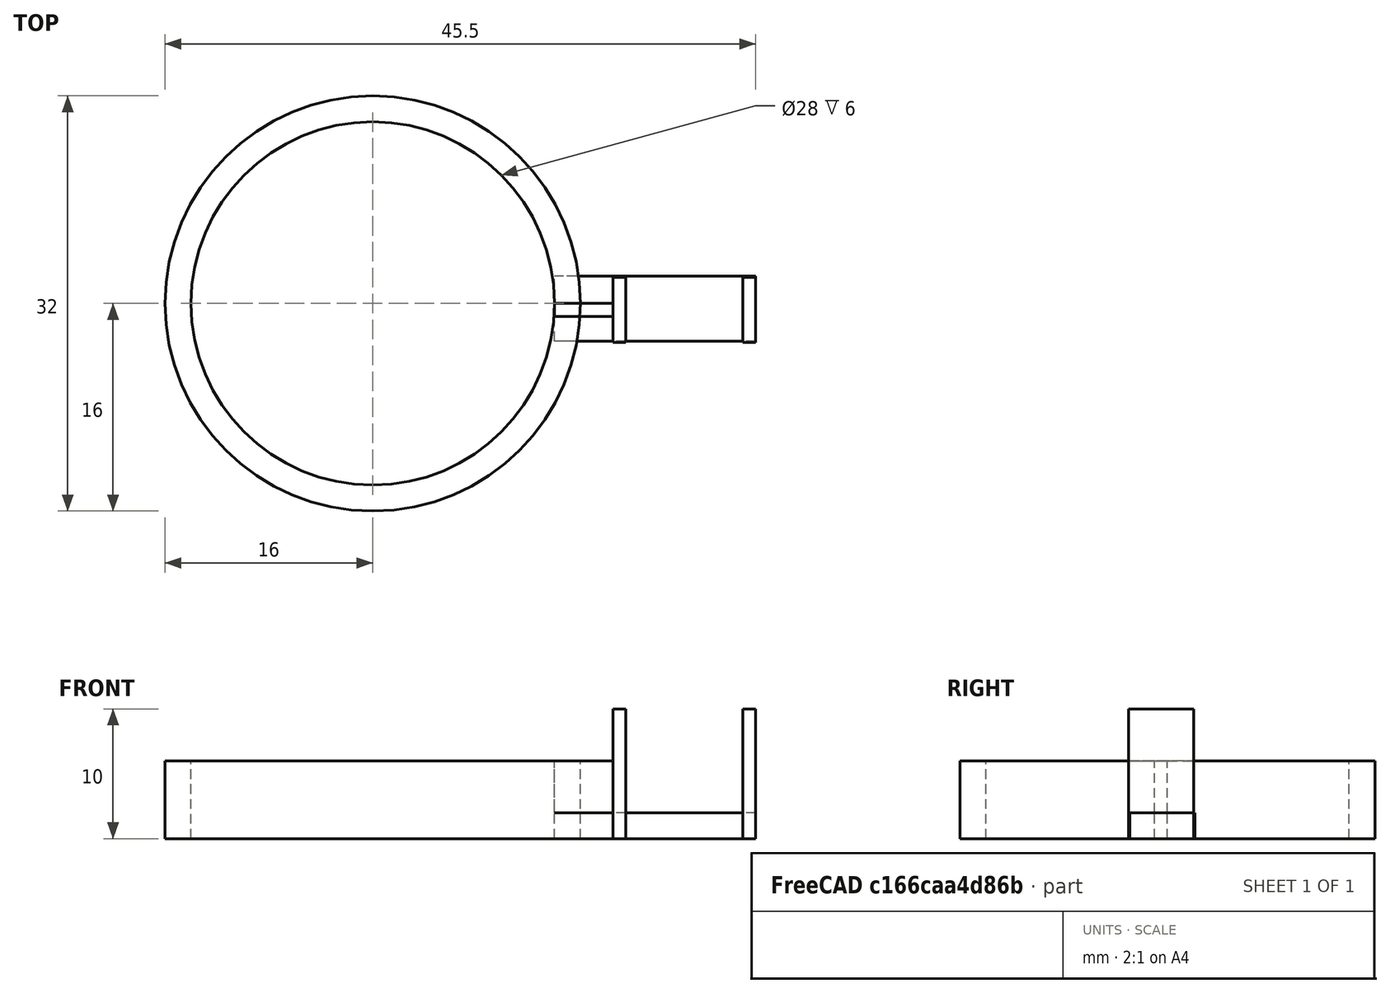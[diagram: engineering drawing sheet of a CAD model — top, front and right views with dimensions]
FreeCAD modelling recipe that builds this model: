
FCSTD DOCUMENT  (FreeCAD 0.18R16117 (Git))
Label: tf2
License: All rights reserved
LicenseURL: http://en.wikipedia.org/wiki/All_rights_reserved
objects: App::MeasureDistance×7, Part::Box×4, Part::Cylinder×2, Part::Cut×1, Part::FeaturePython×1, Part::Mirroring×1
note: 9 computed .brp shape members not serialized (recipe doc carries the construction recipe); baked Part::Feature solids carry a one-line shape summary decoded from their .brp

FEATURE [Part::Cylinder] Cylinder  label="Outer"
  Angle = 360
  AttacherType = Attacher::AttachEngine3D
  Height = 6
  Radius = 16
FEATURE [Part::Cylinder] Cylinder001  label="Inner"
  Angle = 360
  AttacherType = Attacher::AttachEngine3D
  Height = 6
  Radius = 14
FEATURE [Part::Cut] Cut  label="Ring"
  Base = -> Cylinder
  Tool = -> Cylinder001
FEATURE [Part::Box] Box002  label="Cube002"
  AttacherType = Attacher::AttachEngine3D
  Height = 10
  Length = 1
  Placement = pos=(-24,-3,0) rot=(0,0,1;0rad)
  Width = 5
FEATURE [Part::Box] Box003  label="Cube003"
  AttacherType = Attacher::AttachEngine3D
  Height = 6
  Length = 1
  Placement = pos=(-23,7e-15,0) rot=(0,0,-1;1.5708rad)
  Width = 4.5
FEATURE [Part::Box] Box  label="Cube"
  AttacherType = Attacher::AttachEngine3D
  Height = 2
  Length = 15.5
  Placement = pos=(-34,-2.9,0) rot=(0,0,1;0rad)
  Width = 5
FEATURE [Part::Box] Box001  label="Cube001"
  AttacherType = Attacher::AttachEngine3D
  Height = 10
  Length = 1
  Placement = pos=(-34,-3,0) rot=(0,0,1;0rad)
  Width = 5
FEATURE [App::MeasureDistance] Distance  label="Distance: 28.01 mm"
  Distance = 28.012
  P1 = (-14.0661,-1,6)
  P2 = (13.9458,-0.947253,6)
FEATURE [Part::FeaturePython] BooleanFragments  # WARN: FeaturePython — macro-defined, semantics opaque (R4)
  Mode = 0
  Objects = -> [Box003,Box001,Box002,Box]
  Placement = pos=(4.5,0,0) rot=(0,0,1;0rad)
  Tolerance = 0
FEATURE [Part::Mirroring] Part__Mirroring  label="BooleanFragments (Mirror #1)"
  Base = (0,0,0)
  Normal = (1,0,0)
  Source = -> BooleanFragments
FEATURE [App::MeasureDistance] Distance001  label="Distance: 39.00 mm"
  Distance = 39.0002
  P1 = (-19.5,-0.925723,10)
  P2 = (19.5,-1.06463,10)
FEATURE [App::MeasureDistance] Distance002  label="Distance: 57.04 mm"
  Distance = 57.0419
  P1 = (-28.5,0.856895,10)
  P2 = (28.5,-1.32842,10)
FEATURE [App::MeasureDistance] Distance003  label="Distance: 9.05 mm"
  Distance = 9.04741
  P1 = (-28.5,-3,6.55145)
  P2 = (-19.4766,-3,5.89244)
FEATURE [App::MeasureDistance] Distance004  label="Distance: 28.11 mm"
  Distance = 28.107
  P1 = (-14,-1,6)
  P2 = (14.107,-1,6)
FEATURE [App::MeasureDistance] Distance005  label="Distance: 10.00 mm"
  Distance = 10.0033
  P1 = (-29.0816,-3,0)
  P2 = (-28.8238,-3,10)
FEATURE [App::MeasureDistance] Distance006  label="Distance: 5.00 mm"
  Distance = 5.00185
  P1 = (-29.1012,-3,10)
  P2 = (-28.9651,2,10)
